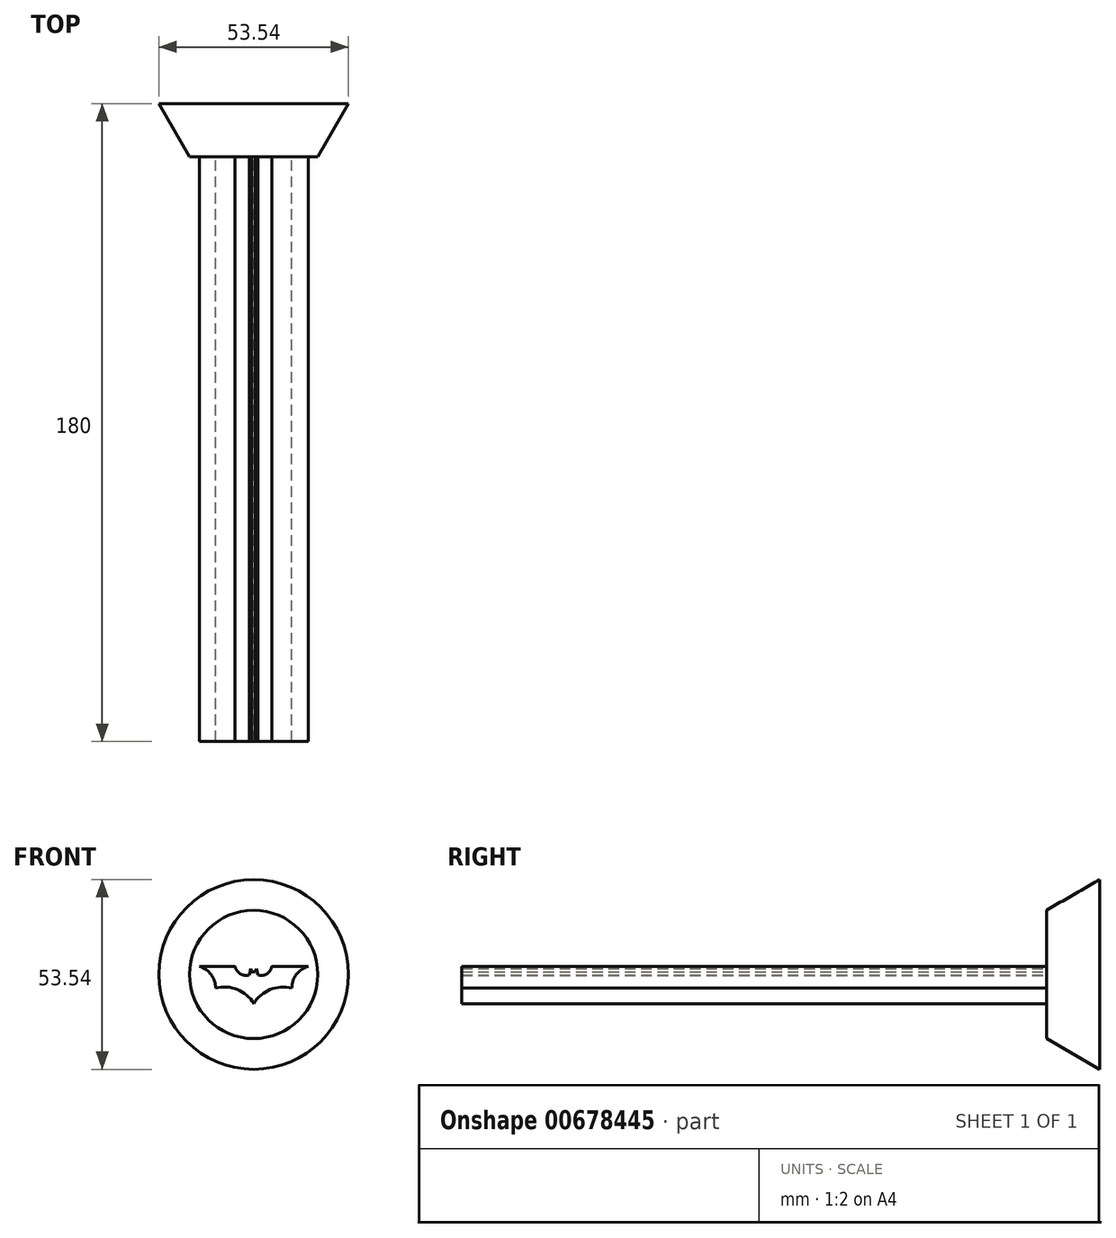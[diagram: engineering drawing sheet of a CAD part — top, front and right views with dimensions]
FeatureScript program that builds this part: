
annotation { "Feature Type Name" : "Feature", "Feature Type Description" : "" }
export const myFeature = defineFeature(function(context is Context, id is Id, definition is map)
    precondition{}
    {
        {
            var Q0;
            Q0=qCreatedBy(makeId("Front.planeOp"),FACE);
            var sketch = newSketch(context, id + "F0", { "sketchPlane" : qUnion([Q0])});
            skLineSegment(sketch, "E0", {"start": v(-15.35, 2.29) * mm, "end": v(-5.22, 2.29) * mm});
            skLineSegment(sketch, "E1", {"start": v(5.09, 2.29) * mm, "end": v(15.4, 2.29) * mm});
            skLineSegment(sketch, "E2", {"start": v(-0.86, 1.69) * mm, "end": v(-1.2, -0.12) * mm});
            skLineSegment(sketch, "E3", {"start": v(0.85, 1.69) * mm, "end": v(1.25, -0.12) * mm});
            skLineSegment(sketch, "E4", {"start": v(-0.86, 1.69) * mm, "end": v(-0.52, 0.75) * mm});
            skLineSegment(sketch, "E5", {"start": v(-0.52, 0.75) * mm, "end": v(0.48, 0.75) * mm});
            skLineSegment(sketch, "E6", {"start": v(0.48, 0.75) * mm, "end": v(0.85, 1.69) * mm});
            skArc(sketch, "E7", {"start": v(-5.22, 2.29) * mm, "mid": v(-3.76, 0.16) * mm, "end": v(-1.2, -0.12) * mm});
            skArc(sketch, "E8", {"start": v(1.25, -0.12) * mm, "mid": v(3.75, 0.16) * mm, "end": v(5.09, 2.29) * mm});
            skArc(sketch, "E9", {"start": v(-10.75, -3.88) * mm, "mid": v(-12.01, -0.02) * mm, "end": v(-15.35, 2.29) * mm});
            skArc(sketch, "E10", {"start": v(15.4, 2.29) * mm, "mid": v(12.04, -0.01) * mm, "end": v(10.78, -3.88) * mm});
            skArc(sketch, "E11", {"start": v(0.03, -8.23) * mm, "mid": v(-4.62, -4.24) * mm, "end": v(-10.75, -3.88) * mm});
            skArc(sketch, "E12", {"start": v(10.78, -3.88) * mm, "mid": v(4.68, -4.26) * mm, "end": v(0.03, -8.23) * mm});
            skSolve(sketch);
        }
        {
            var Q0;
            Q0=makeQuery(id+"F0.imprint","IMPRINT",FACE,{"disambiguationData":[TD([[makeQuery(id+"F0.imprint","IMPRINT",EDGE,{"derivedFrom":sQuery(id+"F0.wireOp",EDGE,"E0")}),-1.0]])]});
            extrude(context, id + "F1", {"entities" : qUnion([Q0]), "depth" : 165 * mm, "offsetDistance" : 25 * mm});
        }
        {
            var Q0;
            Q0=makeQuery(id+"F1.opExtrude","CAP_FACE",FACE,{"disambiguationData":[OSD([sQuery(id+"F0.wireOp",EDGE,"E0"),sQuery(id+"F0.wireOp",EDGE,"E1"),sQuery(id+"F0.wireOp",EDGE,"E2"),sQuery(id+"F0.wireOp",EDGE,"E3"),sQuery(id+"F0.wireOp",EDGE,"E4"),sQuery(id+"F0.wireOp",EDGE,"E5"),sQuery(id+"F0.wireOp",EDGE,"E6"),sQuery(id+"F0.wireOp",EDGE,"E7"),sQuery(id+"F0.wireOp",EDGE,"E8"),sQuery(id+"F0.wireOp",EDGE,"E9"),sQuery(id+"F0.wireOp",EDGE,"E10"),sQuery(id+"F0.wireOp",EDGE,"E11"),sQuery(id+"F0.wireOp",EDGE,"E12")])],"isStart":true});
            var sketch = newSketch(context, id + "F2", { "sketchPlane" : qUnion([Q0])});
            skCircle(sketch, "E13", {"center": v(0, 0) * mm, "radius": 18.1 * mm});
            skSolve(sketch);
        }
        {
            var Q0;
            Q0 = qSketchRegion(id + "F2", true);
            extrude(context, id + "F3", {"entities" : qUnion([Q0]), "operationType" : NewBodyOperationType.ADD, "depth" : 15 * mm, "offsetDistance" : 25 * mm, "hasDraft" : true, "draftAngle" : 30 * degree});
        }
    });
